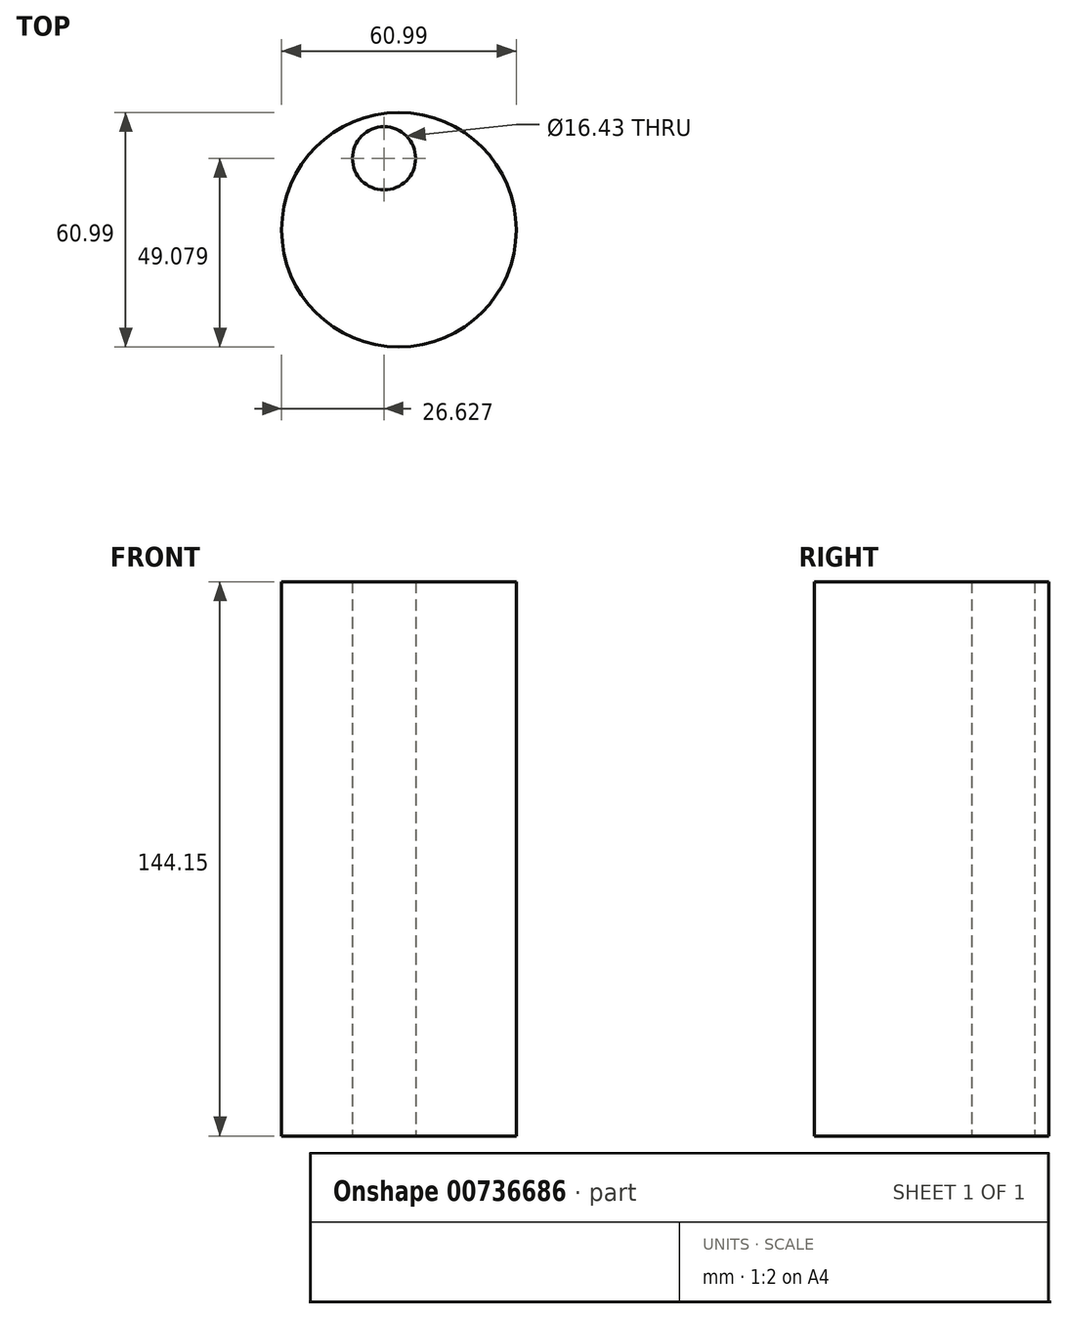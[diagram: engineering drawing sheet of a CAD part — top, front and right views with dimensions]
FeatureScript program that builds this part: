
annotation { "Feature Type Name" : "Feature", "Feature Type Description" : "" }
export const myFeature = defineFeature(function(context is Context, id is Id, definition is map)
    precondition{}
    {
        {
            var Q0;
            Q0=qCreatedBy(makeId("Top.planeOp"),FACE);
            var sketch = newSketch(context, id + "F0", { "sketchPlane" : qUnion([Q0])});
            skCircle(sketch, "E0", {"center": v(-17.42, 12.78) * mm, "radius": 30.5 * mm});
            skCircle(sketch, "E1", {"center": v(-21.3, 31.36) * mm, "radius": 8.21 * mm});
            skSolve(sketch);
        }
        {
            var Q0;
            Q0=makeQuery(id+"F0.imprint","IMPRINT",FACE,{"disambiguationData":[TD([[makeQuery(id+"F0.imprint","IMPRINT",EDGE,{"derivedFrom":sQuery(id+"F0.wireOp",EDGE,"E0")}),1.0]])]});
            extrude(context, id + "F1", {"entities" : qUnion([Q0]), "depth" : 144.14 * mm, "offsetDistance" : 25.4 * mm});
        }
    });
